# Revit family: 09440189
name_source: partatom
category: Plumbing Fixtures
units: mm (PartAtom-declared; Revit-internal decimal feet)

## family parameters
Always vertical = Yes
Cut with Voids When Loaded = No
OmniClass Number = 23.45.55.00
OmniClass Title = Sanitary Faucets, Wastes
Part Type = Normal
Room Calculation Point = No
Round Connector Dimension = Use Diameter
Shared = No
Work Plane-Based = No

## types (1)
- 09440189 Urinal flusher, 6 V, Bluetooth
    2D/3D/BIM Files URL = http://static.hansa.com
    3D View = https://static.hansa.com
    Advanced Features = Software settings adjustable via App
    Afterflush Period = 6 s (1-20 s)
    Ambience photo = http://static.hansa.com
    AssetType = Fixed
    Automatic Flush Frequency = 24 h (off/1-120 h)
    Automatic Flush Period = 6 s (1-120 s)
    AutomaticFlushPeriod = 6.0 s
    BIMObjectName = 09440189
    Battery = Lithium 2CR5 6 V
    BodyMaterial = Brass
    Brand = HANSA
    CO2 Emissions (A1-A3) = 9.7
    CO2 Emissions (A4) = 0.24
    CO2 Emissions (B7) = 88740
    CO2 Emissions (C2) = 0.01
    CO2 Emissions (C3) = 0.01
    CO2 Emissions (C4) = 1.23
    CO2 Emissions (D) = -5.04
    Catalog Drawing URL = http://static.hansa.com
    CloseOffRating = 0
    Color = Chrome
    Connection = Direct connection;Internal thread;with integrated shut-off valve(s)
    Connection Size = G3/4
    Default Elevation = 0 mm  [stored 0 ft]
    Dimension Drawing URL = http://static.hansa.com
    DurationUnit = Year
    EAN Number = 4057304014024
    EMC Directive = Low Voltage Directive 2014/35/EU , 
EMC Directive 2014/30/EU , 
RoHS Directive 2011/65/EU
    EN Standard = EN 15091, ETSI EN 301 489-1 V1.9.2 , 
ETSI EN 300 328 v2.2.2 , 
EN 61000-6-1:2007 , 
EN 61000-6-3:2007+A1:2011+AC:2012 , 
EN 60335-1:2012+A11+A13+A1+A14+A2+A15:2021, Part 19.11.4
    ETIM Class Number = EC010210 Electronic urinal flusher
    Electronic Parts = Autofocus infrared sensor;Solenoid valve;Low battery indicator
    Excluded Items = Without couplings
    FDV Document URL = http://www.hansa.com
    FaucetMainMaterial = Brass
    Features = Touchless;Bluetooth®;Battery-operated
    Finish = Polished
    Flow Drawing URL = http://static.hansa.com
    Flow Rate At 300kPa = 0.6 L/s
    FlowCoefficient = 0
    Group = Urinal flusher
    IfcExportAs = IfcValveType
    IfcExportType = FAUCET
    Installation Type = Wall mounted
    Installation and Maintenance Guide URL = http://static.hansa.com
    Interactive AR View URL = https://static.hansa.com
    Manufacturer = HANSA
    ManufacturerName = HANSA
    ManufacturerURL = http://www.hansa.com
    Market = International;Germany;Austria;Switzerland;Belgium;Netherlands;France;Czech Republic;Slovakia;Hungary;Romania;Italy;Spain;Greece;Portugal;Australia
    Material = Brass
    Max. Hot Water Supply = 70 °C
    Mechanical Parts = Litter filter(s)
    Mobile Product Information URL = http://mpi.hansa.com
    Model = 09440189 Urinal flusher, 6 V, Bluetooth
    ModelReference = 09440189
    NBSDescription = Water supply fittings for baths
    NBSReference = 45-35-70/315
    Name = 09440189 Urinal flusher, 6 V, Bluetooth
    Name_en = 09440189 Urinal flusher, 6 V, Bluetooth
    NominalDepth = 95 mm
    NominalHeight = 260 mm
    NominalWidth = 65 mm
    Operating Distance = 150-400 mm (300/400/500 mm)
    Operating Voltage = 6 V
    Pre-flush Period = 2 s (OFF / 1-10 s)
    Pressure Loss With Flow 02ls = 40000.0 Pa
    Product Code = 09440189
    Product Family = HANSAELECTRA
    Product Image URL = http://static.hansa.com
    Product URL = http://static.hansa.com
    Protection Class = IP 55
    Sales Package dimensions (LxWxH) = 210 x 165 x 60
    Shape = Sculptured
    Size = 65x95x260 mm
    Spare-Part Information URL = http://static.hansa.com
    Spout Projection = 81 mm
    SpoutProjection = 81 mm
    Surface treatment = Chrome
    Technical DataSheet URL = http://www.hansa.com
    UNSPSC Class Number = 30181506 Urinals
    URL Declaration Of Performance (DOP) = http://static.hansa.com
    URL Declaration of Asbestos = http://static.hansa.com
    URL Declaration of Conformity = http://static.hansa.com
    URL Declaration of SCIP = http://static.hansa.com
    URL EU Packaging Declaration = http://static.hansa.com
    URL EcoLabel Declaration = http://static.hansa.com
    URL Environmental Product Declaration EPD = http://www.hansa.com Group EPD_Urinal flusher.pdf
    URL Materials Declaration = http://www.hansa.com
    URL REACH = http://static.hansa.com
    URL UN38.3 = http://static.hansa.com
    URL WEEE = http://static.hansa.com
    Uniclass2 = Pr_40_30_96_07
    Uniclass2015Description = Bath manual water supply sets
    Uniclass2015Reference = Pr_40_20_87_07
    Version = 1
    VersionDate = 01/06/2023
    Warranty Information URL = http://warranty.hansa.com
    WarrantyDescription = http://warranty.hansa.com
    WarrantyDurationUnit = Year
    Working Pressure = 50 - 1000 kPa

note: [stored X ft] marks values corroborated as IEEE doubles in the binary element streams (Revit-internal decimal feet)

## geometry (parser evidence)
native form markers: Sweep x5
no freeform markers — native parametric forms only
